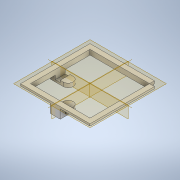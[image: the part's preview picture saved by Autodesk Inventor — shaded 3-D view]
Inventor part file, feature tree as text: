
AUTODESK INVENTOR PART (.ipt)
format: ipt  version: 2022.4 (Build 264492010, 492A)  size: 178,176 bytes
history: native  units: mm
features: extrude x5, sketch x3, chamfer x1, pattern_circular x1
ambient origin geometry x8: Origin, YZ Plane, XZ Plane, XY Plane, X Axis, Y Axis, Z Axis, Center Point
bodies: Solid1 (feature_tree)
feature tree (10):
  sketch  "Sketch1"  dims[d0=60.0mm d1=60.0mm]
  extrude  "Extrusion1"  Depth=60.0mm
  extrude  "Extrusion2"  Depth=2.0mm
  chamfer  "Chamfer1"  Distance=2.0mm
  extrude  "Extrusion3"  Depth=2.0mm TaperAngle=45.0deg
  sketch  "Sketch3"  dims[d6=5.0mm d7=0.0mm d8=3.0mm d9=2.0mm d10=45.0deg d11=10.0mm d12=11.0mm d13=0.0mm d14=10.0mm d15=5.0mm d16=10.0mm d17=3.0mm d19=2.0mm d20=0.0mm d21=4.0mm d22=0.0mm d23=20.0mm d24=-15.707963mm]
  extrude  "Extrusion4"  Depth=10.0mm
  extrude  "Extrusion5"  Depth=11.0mm TaperAngle=0.0deg
  pattern_circular  "Circular Pattern1"  [2 undecoded]
  sketch  "Sketch2"  dims[d2=5.0mm d3=2.0mm d4=2.0mm d5=0.0mm]
note: 2 required parameter values undecoded (feature->parameter linkage not recoverable at this tier; creation-order binding heuristic only, values carry confidence <= 0.55)
